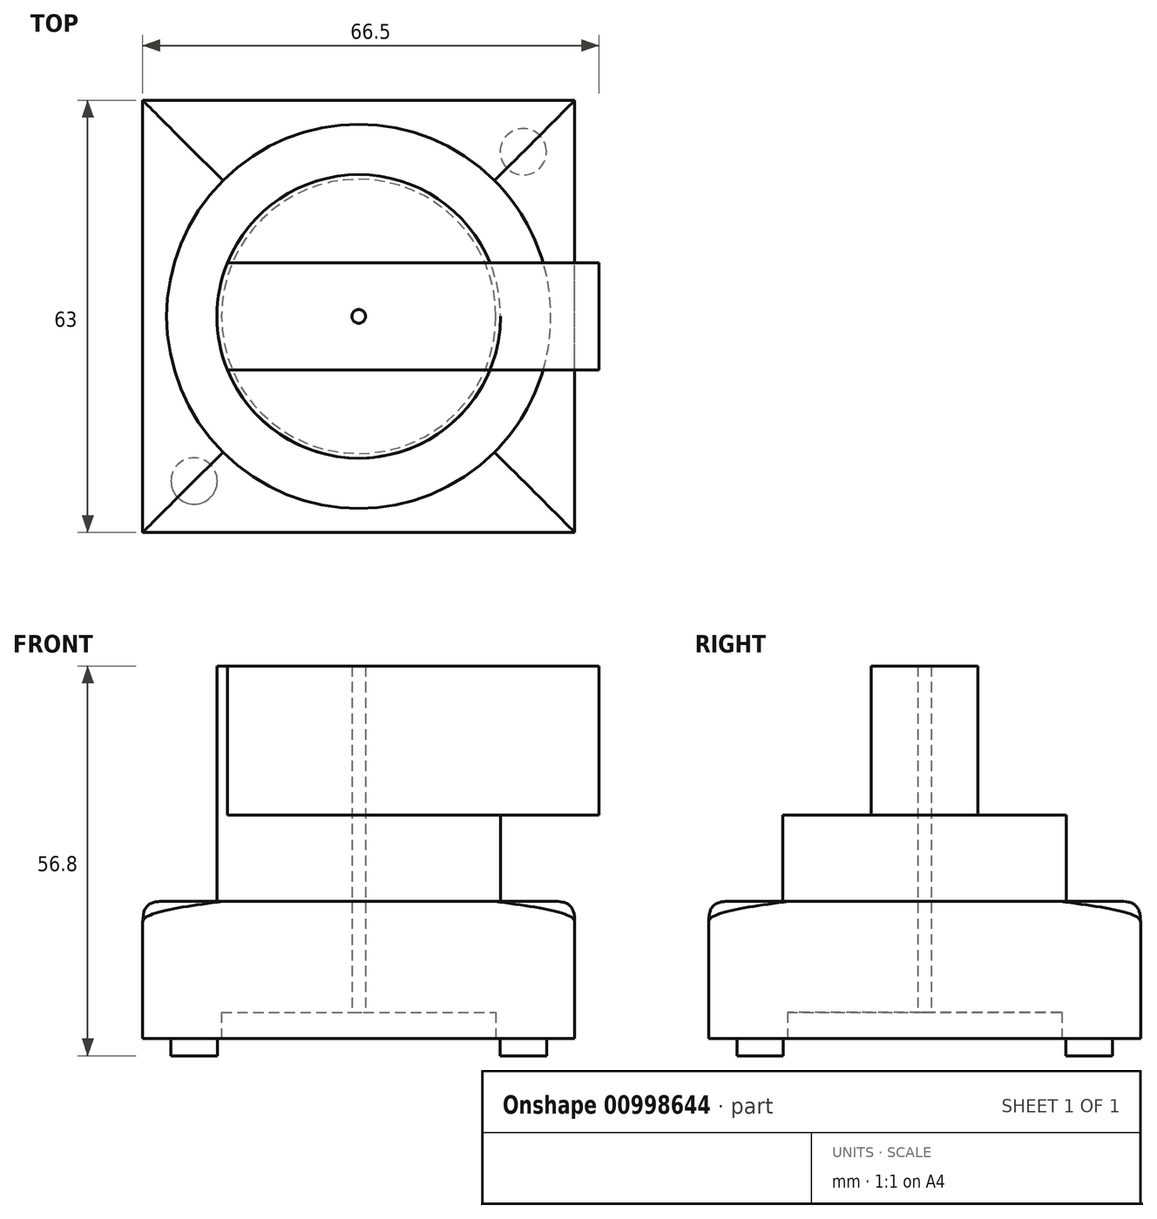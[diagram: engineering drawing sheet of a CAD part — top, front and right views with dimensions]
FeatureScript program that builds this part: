
annotation { "Feature Type Name" : "Feature", "Feature Type Description" : "" }
export const myFeature = defineFeature(function(context is Context, id is Id, definition is map)
    precondition{}
    {
        {
            var Q0;
            Q0=qCreatedBy(makeId("Top.planeOp"),FACE);
            var sketch = newSketch(context, id + "F0", { "sketchPlane" : qUnion([Q0])});
            skLineSegment(sketch, "E0.bottom", {"start": v(31.5, -31.5) * mm, "end": v(-31.5, -31.5) * mm});
            skLineSegment(sketch, "E0.top", {"start": v(31.5, 31.5) * mm, "end": v(-31.5, 31.5) * mm});
            skLineSegment(sketch, "E0.left", {"start": v(31.5, -31.5) * mm, "end": v(31.5, 31.5) * mm});
            skLineSegment(sketch, "E0.right", {"start": v(-31.5, -31.5) * mm, "end": v(-31.5, 31.5) * mm});
            skPoint(sketch, "E0.middle", {"position": v(0, 0) * mm});
            skSolve(sketch);
        }
        {
            var Q0;
            Q0 = qSketchRegion(id + "F0", true);
            extrude(context, id + "F1", {"entities" : qUnion([Q0]), "depth" : 17 * mm, "offsetDistance" : 25 * mm});
        }
        {
            var Q0;
            Q0=makeQuery(id+"F1.opExtrude","CAP_FACE",FACE,{"disambiguationData":[OSD([sQuery(id+"F0.wireOp",EDGE,"E0.bottom"),sQuery(id+"F0.wireOp",EDGE,"E0.top"),sQuery(id+"F0.wireOp",EDGE,"E0.left"),sQuery(id+"F0.wireOp",EDGE,"E0.right")])],"isStart":false});
            cPlane(context, id + "F2", {"entities" : qUnion([Q0]), "cplaneType" : CPlaneType.OFFSET, "offset" : 3 * mm, "width" : 150 * mm, "height" : 150 * mm});
        }
        {
            var Q0;
            Q0=qCreatedBy(id+"F2.planeOp",FACE);
            var sketch = newSketch(context, id + "F3", { "sketchPlane" : qUnion([Q0])});
            skCircle(sketch, "E1", {"center": v(0, 0) * mm, "radius": 28 * mm});
            skSolve(sketch);
        }
        {
            var Q1;
            Q1=makeQuery(id+"F1.opExtrude","CAP_FACE",FACE,{"disambiguationData":[OSD([sQuery(id+"F0.wireOp",EDGE,"E0.bottom"),sQuery(id+"F0.wireOp",EDGE,"E0.top"),sQuery(id+"F0.wireOp",EDGE,"E0.left"),sQuery(id+"F0.wireOp",EDGE,"E0.right")])],"isStart":false});
            var Q2;
            Q2=makeQuery(id+"F3.imprint","IMPRINT",FACE,{"disambiguationData":[TD([[makeQuery(id+"F3.imprint","IMPRINT",EDGE,{"derivedFrom":sQuery(id+"F3.wireOp",EDGE,"E1")}),1.0]])]});
            loft(context, id + "F4", {"operationType" : NewBodyOperationType.ADD, "startCondition" : LoftEndDerivativeType.MATCH_TANGENT, "startMagnitude" : 1, "sheetProfilesArray" : [{ "sheetProfileEntities" : qUnion([Q1]) }, { "sheetProfileEntities" : qUnion([Q2]) }]});
        }
        {
            var Q0;
            Q0=makeQuery(id+"F1.opExtrude","CAP_FACE",FACE,{"disambiguationData":[OSD([sQuery(id+"F0.wireOp",EDGE,"E0.bottom"),sQuery(id+"F0.wireOp",EDGE,"E0.top"),sQuery(id+"F0.wireOp",EDGE,"E0.left"),sQuery(id+"F0.wireOp",EDGE,"E0.right")])],"isStart":true});
            var sketch = newSketch(context, id + "F5", { "sketchPlane" : qUnion([Q0])});
            skCircle(sketch, "E2", {"center": v(24, -24) * mm, "radius": 3.38 * mm});
            skCircle(sketch, "E3", {"center": v(-24, 24) * mm, "radius": 3.38 * mm});
            skCircle(sketch, "E4", {"center": v(0, 0) * mm, "radius": 20 * mm});
            skSolve(sketch);
        }
        {
            var Q0;
            Q0=makeQuery(id+"F5.imprint","IMPRINT",FACE,{"disambiguationData":[TD([[makeQuery(id+"F5.imprint","IMPRINT",EDGE,{"derivedFrom":sQuery(id+"F5.wireOp",EDGE,"E3")}),1.0]])]});
            var Q1;
            Q1=makeQuery(id+"F5.imprint","IMPRINT",FACE,{"disambiguationData":[TD([[makeQuery(id+"F5.imprint","IMPRINT",EDGE,{"derivedFrom":sQuery(id+"F5.wireOp",EDGE,"E2")}),1.0]])]});
            extrude(context, id + "F6", {"entities" : qUnion([Q0, Q1]), "operationType" : NewBodyOperationType.ADD, "depth" : 2.5 * mm, "offsetDistance" : 25 * mm});
        }
        {
            var Q0;
            Q0=makeQuery(id+"F5.imprint","IMPRINT",FACE,{"disambiguationData":[TD([[makeQuery(id+"F5.imprint","IMPRINT",EDGE,{"derivedFrom":sQuery(id+"F5.wireOp",EDGE,"E4")}),1.0]])]});
            extrude(context, id + "F7", {"entities" : qUnion([Q0]), "operationType" : NewBodyOperationType.REMOVE, "oppositeDirection" : true, "depth" : 3.8 * mm, "offsetDistance" : 25 * mm});
        }
        {
            var Q0;
            Q0=makeQuery(id+"F4.opLoft","CAP_FACE",FACE,{"disambiguationData":[OSD([makeQuery(id+"F3.imprint","IMPRINT",FACE,{"disambiguationData":[TD([[makeQuery(id+"F3.imprint","IMPRINT",EDGE,{"derivedFrom":sQuery(id+"F3.wireOp",EDGE,"E1")}),1.0]])]})])],"isStart":true});
            var sketch = newSketch(context, id + "F8", { "sketchPlane" : qUnion([Q0])});
            skCircle(sketch, "E5", {"center": v(0, 0) * mm, "radius": 20.68 * mm});
            skSolve(sketch);
        }
        {
            var Q0;
            Q0=makeQuery(id+"F8.imprint","IMPRINT",FACE,{"disambiguationData":[TD([[makeQuery(id+"F8.imprint","IMPRINT",EDGE,{"derivedFrom":sQuery(id+"F8.wireOp",EDGE,"E5")}),1.0]])]});
            extrude(context, id + "F9", {"entities" : qUnion([Q0]), "operationType" : NewBodyOperationType.ADD, "depth" : 12.6 * mm, "offsetDistance" : 25 * mm});
        }
        {
            var Q0;
            Q0=makeQuery(id+"F9.opExtrude","CAP_FACE",FACE,{"disambiguationData":[OSD([sQuery(id+"F8.wireOp",EDGE,"E5")])],"isStart":false});
            var sketch = newSketch(context, id + "F10", { "sketchPlane" : qUnion([Q0])});
            skLineSegment(sketch, "E6.bottom", {"start": v(21, -7.8) * mm, "end": v(-21, -7.8) * mm});
            skLineSegment(sketch, "E6.top", {"start": v(21, 7.8) * mm, "end": v(-21, 7.8) * mm});
            skLineSegment(sketch, "E6.left", {"start": v(21, -7.8) * mm, "end": v(21, 7.8) * mm});
            skLineSegment(sketch, "E6.right", {"start": v(-21, -7.8) * mm, "end": v(-21, 7.8) * mm});
            skPoint(sketch, "E6.middle", {"position": v(0, 0) * mm});
            skSolve(sketch);
        }
        {
            var Q0;
            {var subQ0=sQuery(id+"F10.wireOp",EDGE,"E6.bottom");var subQ1=makeQuery(id+"F9.opExtrude","CAP_EDGE",EDGE,{"disambiguationData":[OSD([sQuery(id+"F8.wireOp",EDGE,"E5")])],"isStart":false});var subQ2=makeQuery(id+"F10.imprint","INTERSECT",VERTEX,{"disambiguationData":[OD(0.0)],"derivedFrom":[subQ1,subQ0]});Q0=makeQuery(id+"F10.imprint","IMPRINT",FACE,{"disambiguationData":[TD([[makeQuery(id+"F10.imprint","IMPRINT",EDGE,{"disambiguationData":[TD([[subQ2,-1.0]])],"derivedFrom":subQ0}),-1.0]])]});}
            var Q1;
            {var subQ0=sQuery(id+"F10.wireOp",EDGE,"E6.left");Q1=makeQuery(id+"F10.imprint","IMPRINT",FACE,{"disambiguationData":[TD([[makeQuery(id+"F10.imprint","IMPRINT",EDGE,{"derivedFrom":subQ0}),1.0]])]});}
            extrude(context, id + "F11", {"entities" : qUnion([Q0, Q1]), "operationType" : NewBodyOperationType.ADD, "depth" : 21.7 * mm, "offsetDistance" : 25 * mm});
        }
        {
            var Q0;
            Q0=makeQuery(id+"F11.opExtrude","SWEPT_FACE",FACE,{"disambiguationData":[OSD([sQuery(id+"F10.wireOp",EDGE,"E6.left")])]});
            extrude(context, id + "F12", {"entities" : qUnion([Q0]), "operationType" : NewBodyOperationType.ADD, "depth" : 14 * mm, "offsetDistance" : 25 * mm});
        }
        {
            var Q0;
            Q0=makeQuery(id+"F7.boolean.opBoolean","COPY",FACE,{"derivedFrom":makeQuery(id+"F7.opExtrude","CAP_FACE",FACE,{"disambiguationData":[OSD([sQuery(id+"F5.wireOp",EDGE,"E4")])],"isStart":false})});
            var sketch = newSketch(context, id + "F13", { "sketchPlane" : qUnion([Q0])});
            skCircle(sketch, "E7", {"center": v(0, 0) * mm, "radius": 1 * mm});
            skSolve(sketch);
        }
        {
            var Q0;
            Q0 = qSketchRegion(id + "F13", true);
            extrude(context, id + "F14", {"entities" : qUnion([Q0]), "operationType" : NewBodyOperationType.REMOVE, "endBound" : BoundingType.THROUGH_ALL, "oppositeDirection" : true, "depth" : 25 * mm, "offsetDistance" : 25 * mm});
        }
    });
